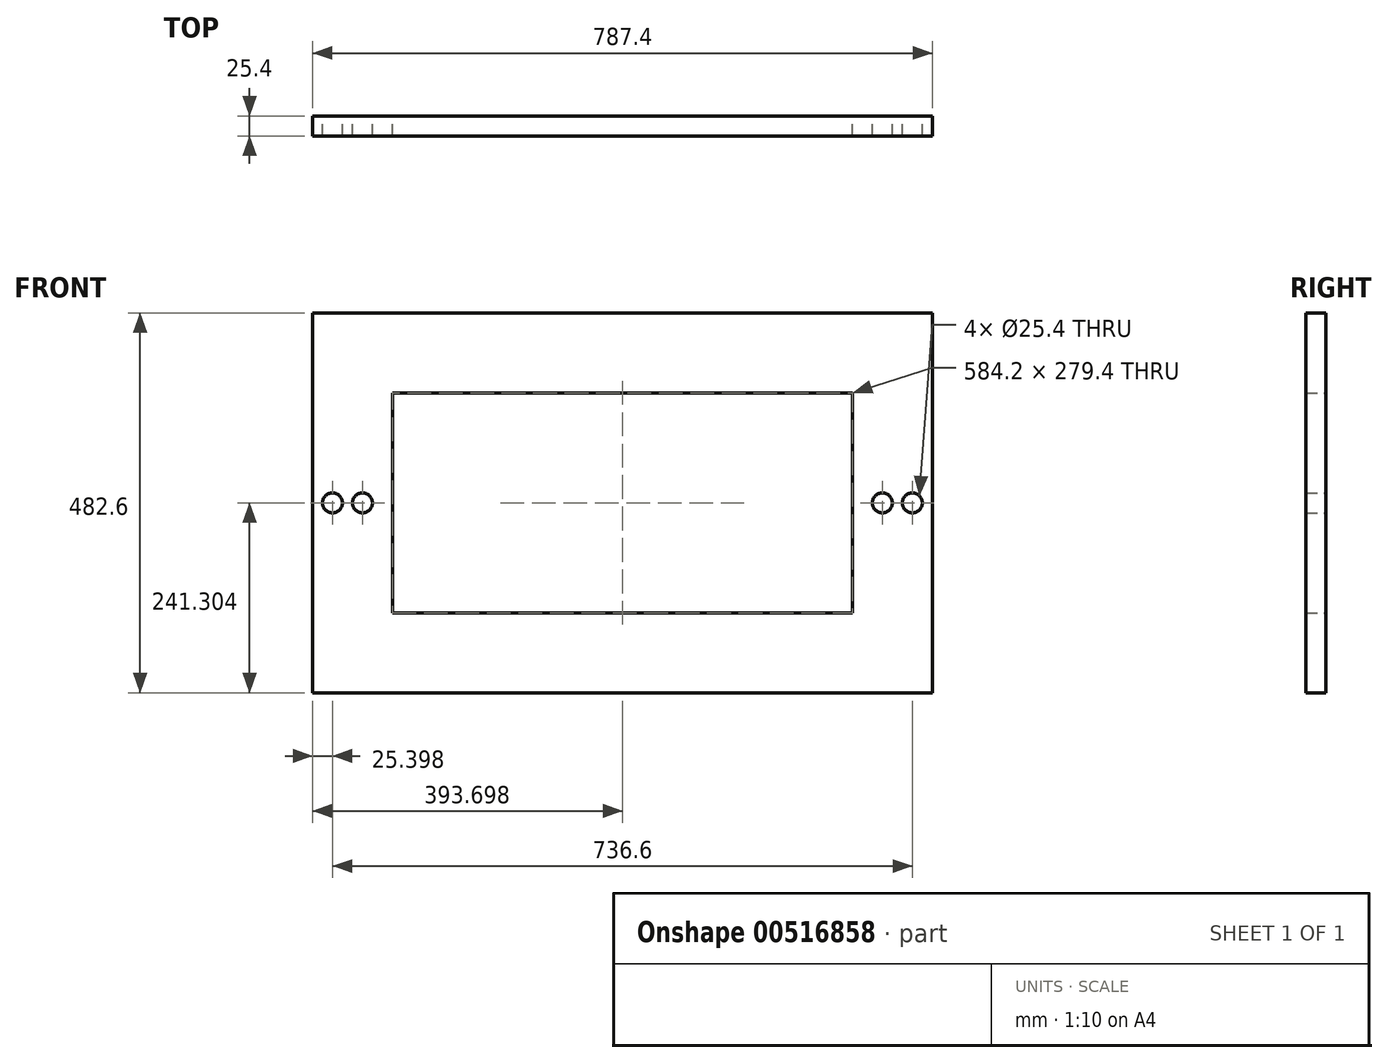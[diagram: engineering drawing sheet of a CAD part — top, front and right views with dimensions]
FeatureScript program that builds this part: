
annotation { "Feature Type Name" : "Feature", "Feature Type Description" : "" }
export const myFeature = defineFeature(function(context is Context, id is Id, definition is map)
    precondition{}
    {
        {
            var Q0;
            Q0=qCreatedBy(makeId("Front.planeOp"),FACE);
            var sketch = newSketch(context, id + "F0", { "sketchPlane" : qUnion([Q0])});
            skLineSegment(sketch, "E0.bottom", {"start": v(18.9, 283.18) * mm, "end": v(603.1, 283.18) * mm});
            skLineSegment(sketch, "E0.top", {"start": v(18.9, 3.78) * mm, "end": v(603.1, 3.78) * mm});
            skLineSegment(sketch, "E0.left", {"start": v(18.9, 283.18) * mm, "end": v(18.9, 3.78) * mm});
            skLineSegment(sketch, "E0.right", {"start": v(603.1, 283.18) * mm, "end": v(603.1, 3.78) * mm});
            skLineSegment(sketch, "E1.bottom", {"start": v(-82.7, 384.78) * mm, "end": v(704.7, 384.78) * mm});
            skLineSegment(sketch, "E1.top", {"start": v(-82.7, -97.82) * mm, "end": v(704.7, -97.82) * mm});
            skLineSegment(sketch, "E1.left", {"start": v(-82.7, 384.78) * mm, "end": v(-82.7, -97.82) * mm});
            skLineSegment(sketch, "E1.right", {"start": v(704.7, 384.78) * mm, "end": v(704.7, -97.82) * mm});
            skCircle(sketch, "E2", {"center": v(641.2, 143.48) * mm, "radius": 12.7 * mm});
            skCircle(sketch, "E3", {"center": v(679.3, 143.48) * mm, "radius": 12.7 * mm});
            skCircle(sketch, "E4", {"center": v(-57.3, 143.48) * mm, "radius": 12.7 * mm});
            skCircle(sketch, "E5", {"center": v(-19.2, 143.48) * mm, "radius": 12.7 * mm});
            skSolve(sketch);
        }
        {
            var Q0;
            Q0 = qSketchRegion(id + "F0", true);
            extrude(context, id + "F1", {"entities" : qUnion([Q0]), "depth" : 25.4 * mm, "offsetDistance" : 25.4 * mm});
        }
    });
